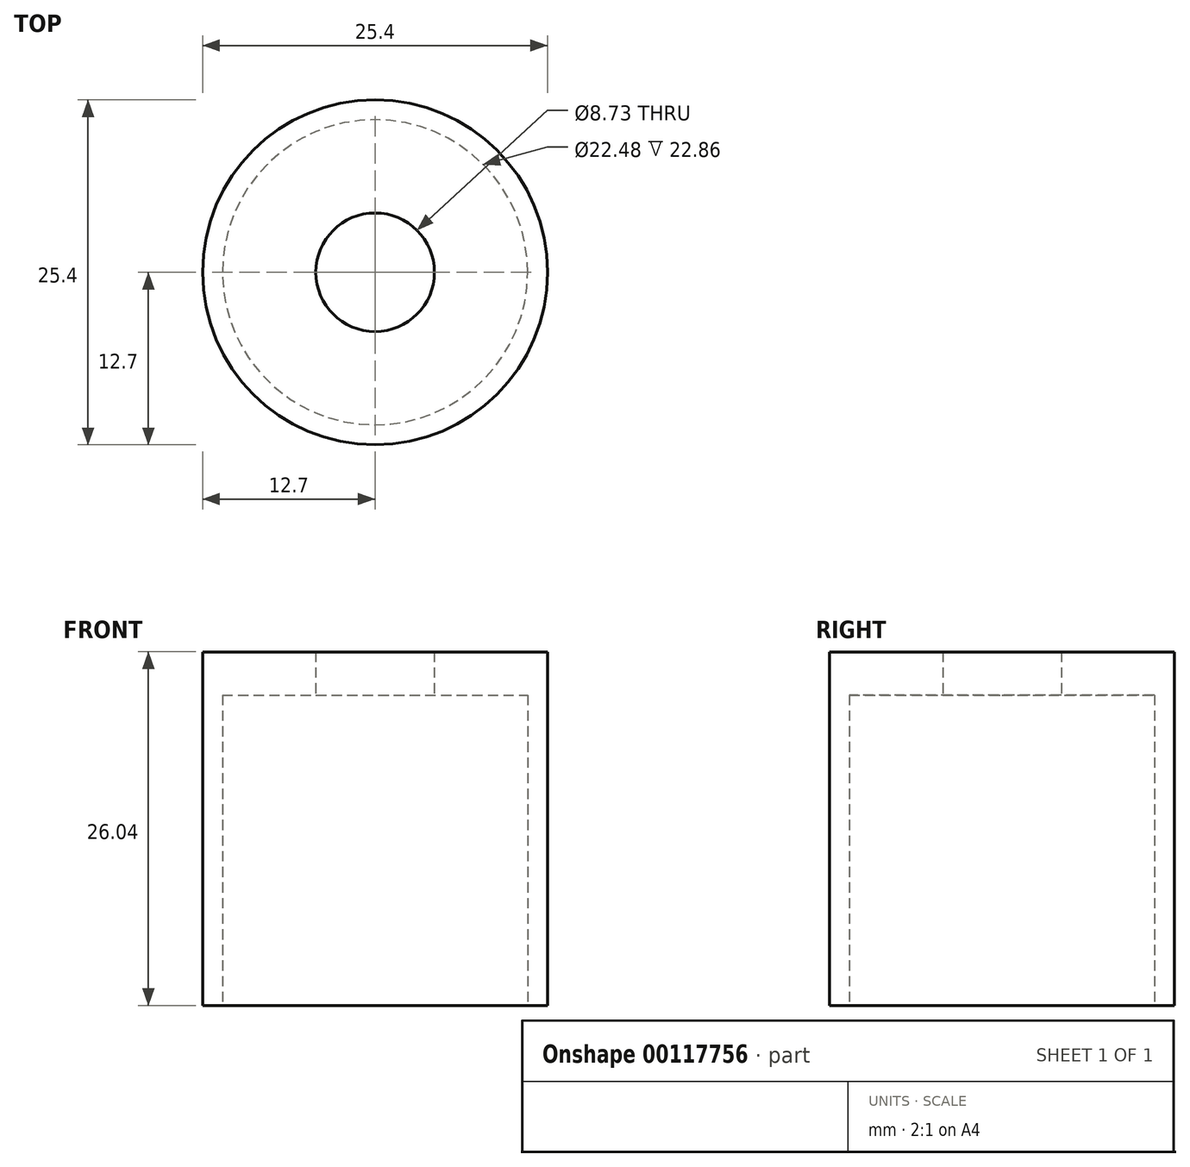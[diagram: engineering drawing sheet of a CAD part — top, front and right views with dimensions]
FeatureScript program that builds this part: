
annotation { "Feature Type Name" : "Feature", "Feature Type Description" : "" }
export const myFeature = defineFeature(function(context is Context, id is Id, definition is map)
    precondition{}
    {
        {
            var Q0;
            Q0=qCreatedBy(makeId("Right.planeOp"),FACE);
            var sketch = newSketch(context, id + "F0", { "sketchPlane" : qUnion([Q0])});
            skLineSegment(sketch, "E0", {"start": v(0, 0) * mm, "end": v(0, 26.04) * mm, "construction": true});
            skLineSegment(sketch, "E1", {"start": v(4.37, 26.04) * mm, "end": v(12.7, 26.04) * mm});
            skLineSegment(sketch, "E2", {"start": v(12.7, 26.04) * mm, "end": v(12.7, 0) * mm});
            skLineSegment(sketch, "E3", {"start": v(12.7, 0) * mm, "end": v(11.24, 0) * mm});
            skLineSegment(sketch, "E4", {"start": v(11.24, 22.86) * mm, "end": v(4.37, 22.86) * mm});
            skLineSegment(sketch, "E5", {"start": v(4.37, 22.86) * mm, "end": v(4.37, 26.04) * mm});
            skLineSegment(sketch, "E6", {"start": v(11.24, 22.86) * mm, "end": v(11.24, 0) * mm});
            skLineSegment(sketch, "E7.MirrorCS", {"start": v(-11.24, 22.86) * mm, "end": v(-11.24, 0) * mm, "construction": true});
            skLineSegment(sketch, "E8.MirrorCS", {"start": v(-4.37, 22.86) * mm, "end": v(-4.37, 26.04) * mm});
            skSolve(sketch);
        }
        {
            var Q0;
            Q0 = qSketchRegion(id + "F0", true);
            var Q1;
            Q1=sQuery(id+"F0.wireOp",EDGE,"E0");
            revolve(context, id + "F1", {"entities" : qUnion([Q0]), "axis" : qUnion([Q1]), "revolveType" : RevolveType.FULL});
        }
    });
